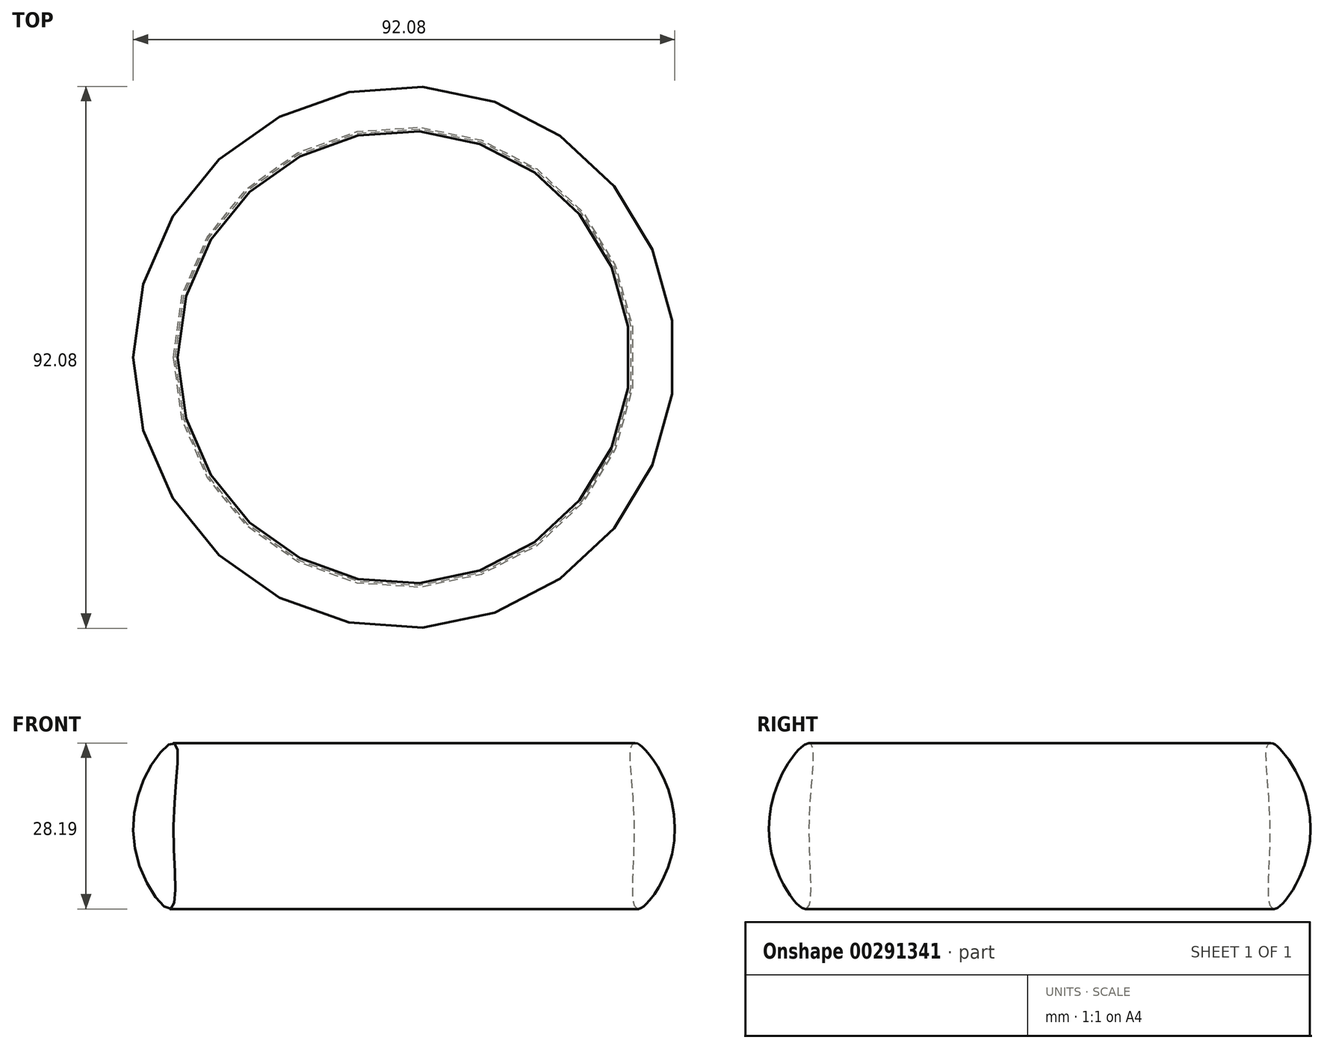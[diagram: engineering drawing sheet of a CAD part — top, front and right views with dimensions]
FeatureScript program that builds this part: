
annotation { "Feature Type Name" : "Feature", "Feature Type Description" : "" }
export const myFeature = defineFeature(function(context is Context, id is Id, definition is map)
    precondition{}
    {
        {
            var Q0;
            Q0=qCreatedBy(makeId("Front.planeOp"),FACE);
            var sketch = newSketch(context, id + "F0", { "sketchPlane" : qUnion([Q0])});
            skLineSegment(sketch, "E0", {"start": v(0, -26.23) * mm, "end": v(0, 27.85) * mm, "construction": true});
            skFitSpline(sketch, "E1", {"points": [v(-39.65, -12.63) * mm, v(-39.17, 1.83) * mm, v(-39.04, 15.49) * mm, v(-43.83, 10.23) * mm, v(-45.04, -5.15) * mm, v(-39.65, -12.63) * mm]});
            skSolve(sketch);
        }
        {
            var Q0;
            Q0 = qSketchRegion(id + "F0", true);
            var Q1;
            Q1=sQuery(id+"F0.wireOp",EDGE,"E0");
            revolve(context, id + "F1", {"entities" : qUnion([Q0]), "axis" : qUnion([Q1]), "revolveType" : RevolveType.FULL});
        }
    });
